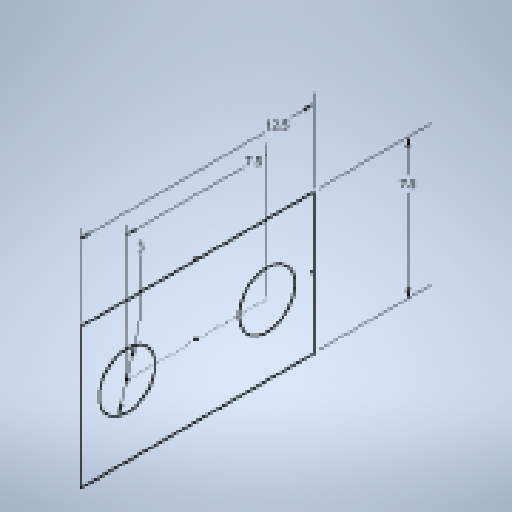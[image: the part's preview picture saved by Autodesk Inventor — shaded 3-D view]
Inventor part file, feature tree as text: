
AUTODESK INVENTOR PART (.ipt)
format: ipt  version: 2023 (Build 270158000, 158)  size: 178,688 bytes
history: native  units: in
note: dims shown in document units (in); Inventor stores cm internally (conversion verified against a paired STEP export)
features: extrude x3, sketch x3, fillet x1
ambient origin geometry x8: Origin, YZ Plane, XZ Plane, XY Plane, X Axis, Y Axis, Z Axis, Center Point
bodies: Solid1 (feature_tree)
feature tree (7):
  extrude  "Extrusion1"  Depth=0.2953in
  extrude  "Extrusion2"  Depth=0.2953in
  extrude  "Extrusion3"  Depth=0.1969in TaperAngle=0.0deg
  fillet  "Fillet1"  Radius=0.3937in
  sketch  "Sketch1"  dims[d0=0.4921in d1=0.2953in]
  sketch  "Sketch2"  dims[d2=0.1181in d3=0.2953in]
  sketch  "Sketch3"  dims[d4=0.1969in d5=0.1969in d6=0.0in d7=0.3937in d8=1.7717in d9=0.1969in d10=0.0in d11=0.4724in d12=0.1575in d13=0.1969in d14=0.0in d15=0.1969in]
